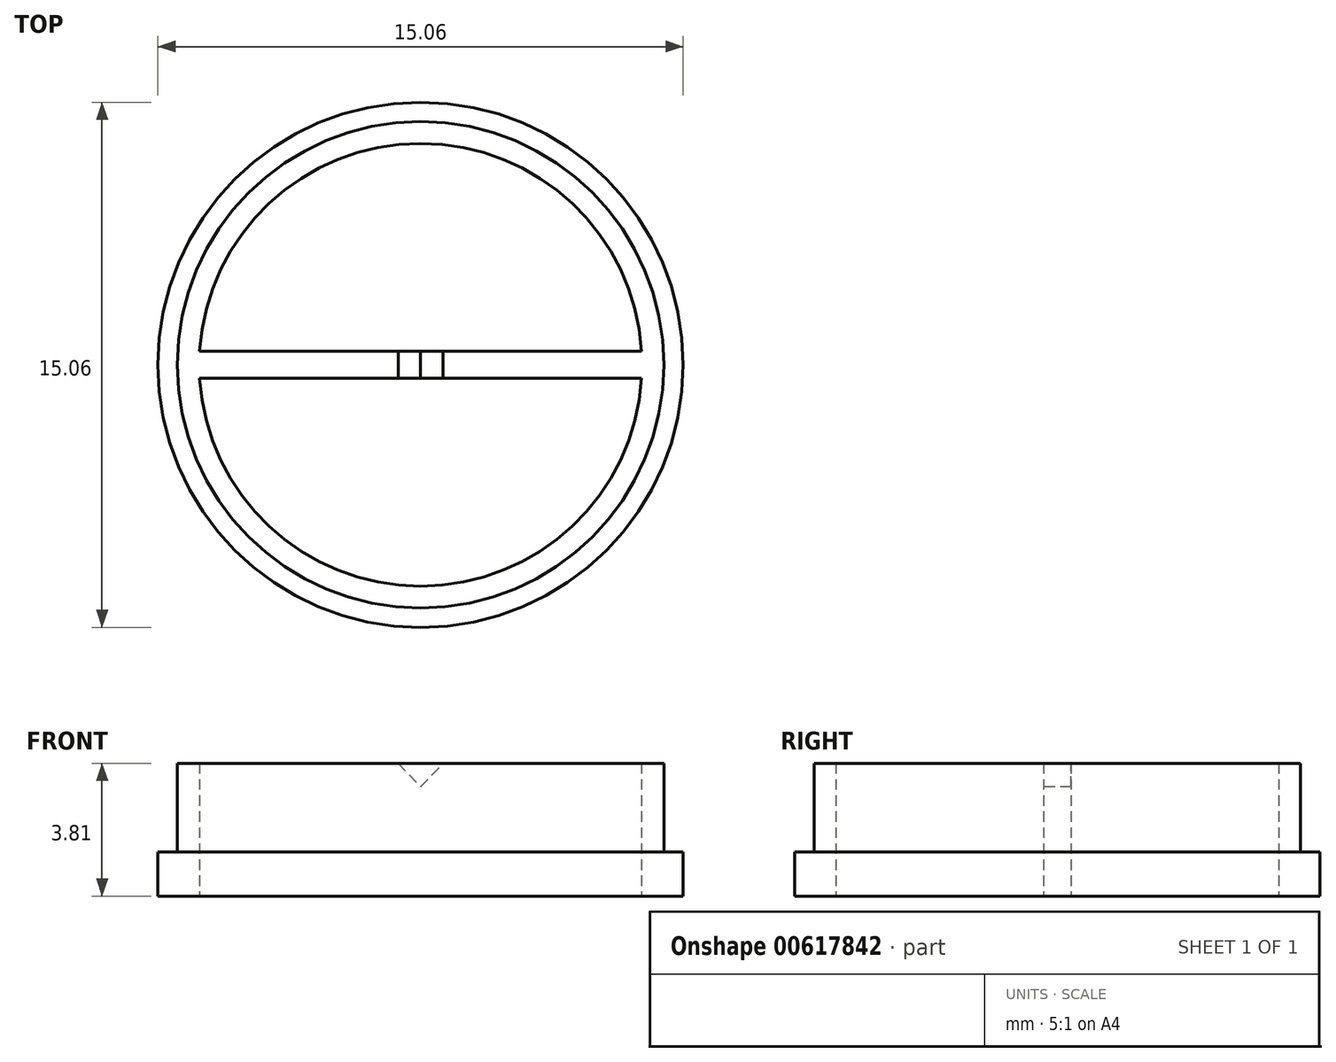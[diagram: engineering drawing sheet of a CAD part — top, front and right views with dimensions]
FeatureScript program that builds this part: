
annotation { "Feature Type Name" : "Feature", "Feature Type Description" : "" }
export const myFeature = defineFeature(function(context is Context, id is Id, definition is map)
    precondition{}
    {
        {
            var Q0;
            Q0=qCreatedBy(makeId("Top.planeOp"),FACE);
            var sketch = newSketch(context, id + "F0", { "sketchPlane" : qUnion([Q0])});
            skCircle(sketch, "E0", {"center": v(0, 0) * mm, "radius": 6.35 * mm});
            skCircle(sketch, "E1", {"center": v(0, 0) * mm, "radius": 7.53 * mm});
            skSolve(sketch);
        }
        {
            var Q0;
            Q0=makeQuery(id+"F0.imprint","IMPRINT",FACE,{"disambiguationData":[TD([[makeQuery(id+"F0.imprint","IMPRINT",EDGE,{"derivedFrom":sQuery(id+"F0.wireOp",EDGE,"E0")}),-1.0]])]});
            extrude(context, id + "F1", {"entities" : qUnion([Q0]), "depth" : 1.27 * mm, "offsetDistance" : 25.4 * mm});
        }
        {
            var Q0;
            Q0=makeQuery(id+"F1.opExtrude","CAP_FACE",FACE,{"disambiguationData":[OSD([sQuery(id+"F0.wireOp",EDGE,"E0"),sQuery(id+"F0.wireOp",EDGE,"E1")])],"isStart":false});
            var sketch = newSketch(context, id + "F2", { "sketchPlane" : qUnion([Q0])});
            skCircle(sketch, "E2", {"center": v(0, 0) * mm, "radius": 6.98 * mm});
            skSolve(sketch);
        }
        {
            var Q0;
            Q0=makeQuery(id+"F2.imprint","IMPRINT",FACE,{"disambiguationData":[TD([[makeQuery(id+"F2.imprint","IMPRINT",EDGE,{"derivedFrom":sQuery(id+"F2.wireOp",EDGE,"E2")}),1.0]])]});
            extrude(context, id + "F3", {"entities" : qUnion([Q0]), "operationType" : NewBodyOperationType.ADD, "depth" : 2.54 * mm, "offsetDistance" : 25.4 * mm});
        }
        {
            var Q0;
            Q0=makeQuery(id+"F3.opExtrude","CAP_FACE",FACE,{"disambiguationData":[OSD([sQuery(id+"F0.wireOp",EDGE,"E0"),sQuery(id+"F2.wireOp",EDGE,"E2")])],"isStart":false});
            var sketch = newSketch(context, id + "F4", { "sketchPlane" : qUnion([Q0])});
            skCircle(sketch, "E3", {"center": v(0, 0) * mm, "radius": 7.18 * mm});
            skCircle(sketch, "E4", {"center": v(0, 0) * mm, "radius": 6.83 * mm});
            skSolve(sketch);
        }
        {
            var Q0;
            Q0=makeQuery(id+"F4.imprint","IMPRINT",FACE,{"disambiguationData":[TD([[makeQuery(id+"F4.imprint","IMPRINT",EDGE,{"derivedFrom":sQuery(id+"F4.wireOp",EDGE,"E4")}),1.0]])]});
            var sketch = newSketch(context, id + "F5", { "sketchPlane" : qUnion([Q0])});
            skLineSegment(sketch, "E5.bottom", {"start": v(6.79, -0.39) * mm, "end": v(-6.79, -0.39) * mm});
            skLineSegment(sketch, "E5.top", {"start": v(6.79, 0.39) * mm, "end": v(-6.79, 0.39) * mm});
            skLineSegment(sketch, "E5.left", {"start": v(6.79, -0.39) * mm, "end": v(6.79, 0.39) * mm});
            skLineSegment(sketch, "E5.right", {"start": v(-6.79, -0.39) * mm, "end": v(-6.79, 0.39) * mm});
            skPoint(sketch, "E5.middle", {"position": v(0, 0) * mm});
            skSolve(sketch);
        }
        {
            var Q0;
            Q0 = qSketchRegion(id + "F5", true);
            extrude(context, id + "F6", {"entities" : qUnion([Q0]), "operationType" : NewBodyOperationType.ADD, "oppositeDirection" : true, "depth" : 3.8 * mm, "offsetDistance" : 25.4 * mm});
        }
        {
            var Q0;
            Q0=makeQuery(id+"F6.opExtrude","SWEPT_FACE",FACE,{"disambiguationData":[OSD([sQuery(id+"F5.wireOp",EDGE,"E5.bottom")])]});
            var sketch = newSketch(context, id + "F7", { "sketchPlane" : qUnion([Q0])});
            skLineSegment(sketch, "E6", {"start": v(0, 3.81) * mm, "end": v(0, 3.13) * mm});
            skPoint(sketch, "E6.endSnap0", {"position": v(0, 3.81) * mm});
            skLineSegment(sketch, "E7", {"start": v(0, 3.13) * mm, "end": v(0.64, 3.81) * mm});
            skLineSegment(sketch, "E8", {"start": v(0.64, 3.81) * mm, "end": v(-0.64, 3.81) * mm});
            skLineSegment(sketch, "E9", {"start": v(-0.64, 3.81) * mm, "end": v(0, 3.13) * mm});
            skSolve(sketch);
        }
        {
            var Q0;
            Q0 = qSketchRegion(id + "F7", true);
            extrude(context, id + "F8", {"entities" : qUnion([Q0]), "operationType" : NewBodyOperationType.REMOVE, "oppositeDirection" : true, "depth" : 2.54 * mm, "offsetDistance" : 25.4 * mm});
        }
    });
